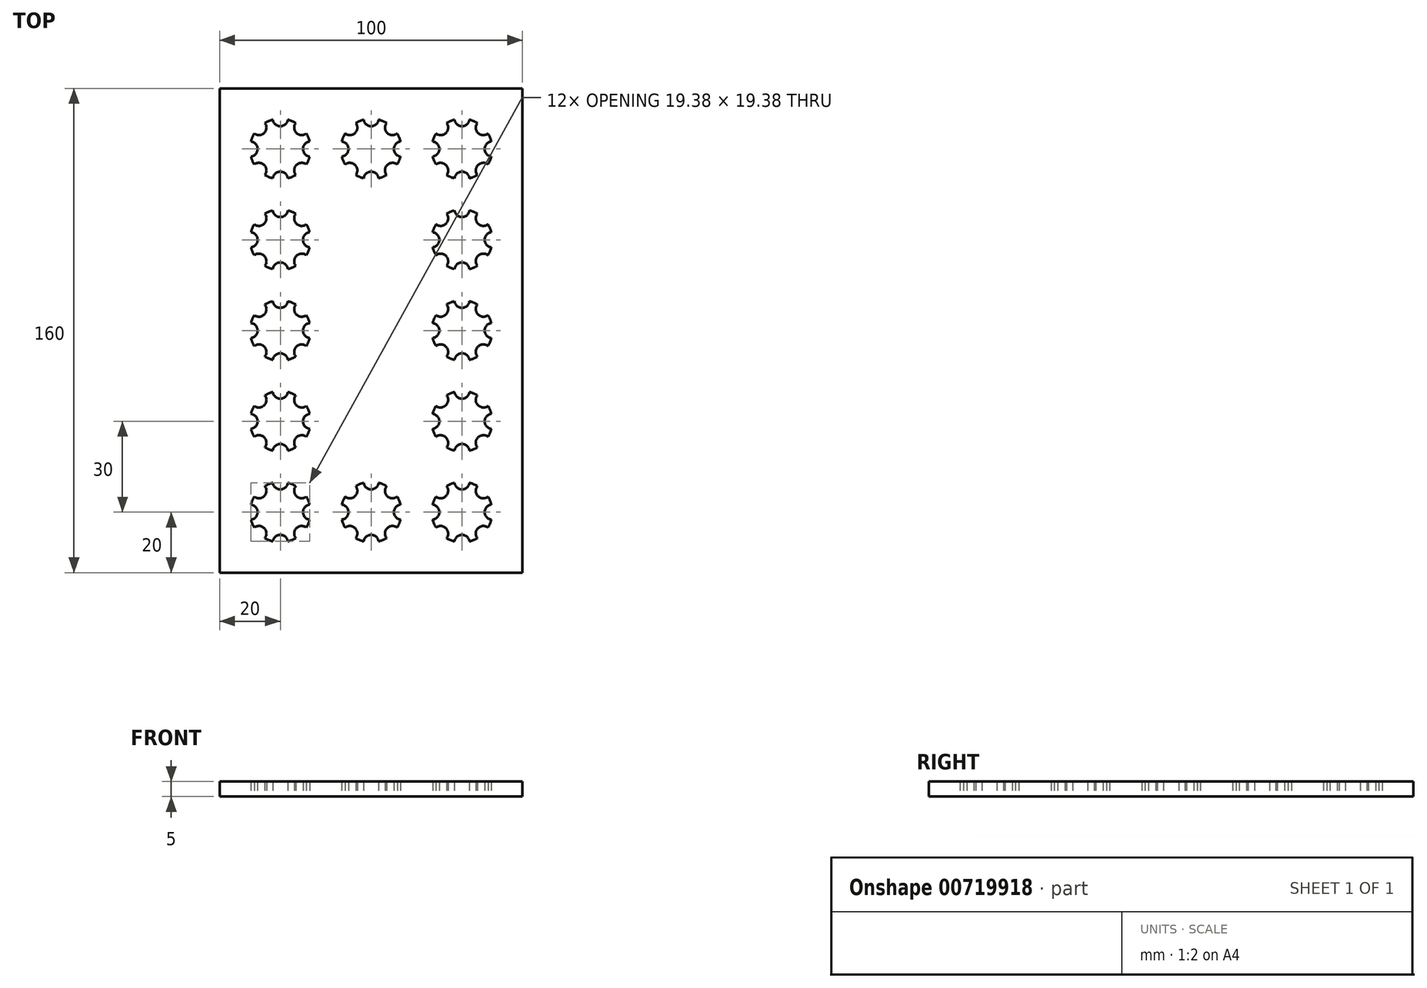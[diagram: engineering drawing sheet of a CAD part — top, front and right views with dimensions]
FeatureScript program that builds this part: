
annotation { "Feature Type Name" : "Feature", "Feature Type Description" : "" }
export const myFeature = defineFeature(function(context is Context, id is Id, definition is map)
    precondition{}
    {
        {
            var Q0;
            Q0=qCreatedBy(makeId("Top.planeOp"),FACE);
            var sketch = newSketch(context, id + "F0", { "sketchPlane" : qUnion([Q0])});
            skLineSegment(sketch, "E0.bottom", {"start": v(0, 0) * mm, "end": v(100, 0) * mm});
            skLineSegment(sketch, "E0.top", {"start": v(0, -160) * mm, "end": v(100, -160) * mm});
            skLineSegment(sketch, "E0.left", {"start": v(0, 0) * mm, "end": v(0, -160) * mm});
            skLineSegment(sketch, "E0.right", {"start": v(100, 0) * mm, "end": v(100, -160) * mm});
            skArc(sketch, "E1", {"start": v(25.1, -11.4) * mm, "mid": v(23.83, -10.76) * mm, "end": v(22.48, -10.31) * mm});
            skArc(sketch, "E2", {"start": v(17.52, -10.31) * mm, "mid": v(20, -12.5) * mm, "end": v(22.48, -10.31) * mm});
            skArc(sketch, "E3.1.0", {"start": v(11.4, -14.9) * mm, "mid": v(14.7, -14.7) * mm, "end": v(14.9, -11.4) * mm});
            skArc(sketch, "E3.2.0", {"start": v(10.31, -22.48) * mm, "mid": v(12.5, -20) * mm, "end": v(10.31, -17.52) * mm});
            skArc(sketch, "E3.3.0", {"start": v(14.9, -28.6) * mm, "mid": v(14.7, -25.3) * mm, "end": v(11.4, -25.1) * mm});
            skArc(sketch, "E3.4.0", {"start": v(22.48, -29.69) * mm, "mid": v(20, -27.5) * mm, "end": v(17.52, -29.69) * mm});
            skArc(sketch, "E3.5.0", {"start": v(28.6, -25.1) * mm, "mid": v(25.3, -25.3) * mm, "end": v(25.1, -28.6) * mm});
            skArc(sketch, "E3.6.0", {"start": v(29.69, -17.52) * mm, "mid": v(27.5, -20) * mm, "end": v(29.69, -22.48) * mm});
            skArc(sketch, "E3.7.0", {"start": v(25.1, -11.4) * mm, "mid": v(25.3, -14.7) * mm, "end": v(28.6, -14.9) * mm});
            skArc(sketch, "E4.trimOffspring", {"start": v(29.69, -17.52) * mm, "mid": v(29.24, -16.17) * mm, "end": v(28.6, -14.9) * mm});
            skArc(sketch, "E5.trimOffspring", {"start": v(28.6, -25.1) * mm, "mid": v(29.24, -23.83) * mm, "end": v(29.69, -22.48) * mm});
            skArc(sketch, "E6.trimOffspring", {"start": v(22.48, -29.69) * mm, "mid": v(23.83, -29.24) * mm, "end": v(25.1, -28.6) * mm});
            skArc(sketch, "E7.trimOffspring", {"start": v(14.9, -28.6) * mm, "mid": v(16.17, -29.24) * mm, "end": v(17.52, -29.69) * mm});
            skArc(sketch, "E8.trimOffspring", {"start": v(10.31, -22.48) * mm, "mid": v(10.76, -23.83) * mm, "end": v(11.4, -25.1) * mm});
            skArc(sketch, "E9.trimOffspring", {"start": v(11.4, -14.9) * mm, "mid": v(10.76, -16.17) * mm, "end": v(10.31, -17.52) * mm});
            skArc(sketch, "E10.trimOffspring", {"start": v(17.52, -10.31) * mm, "mid": v(16.17, -10.76) * mm, "end": v(14.9, -11.4) * mm});
            skArc(sketch, "E11", {"start": v(25.1, -41.4) * mm, "mid": v(23.83, -40.76) * mm, "end": v(22.48, -40.31) * mm});
            skArc(sketch, "E12", {"start": v(17.52, -40.31) * mm, "mid": v(20, -42.5) * mm, "end": v(22.48, -40.31) * mm});
            skArc(sketch, "E13.1.0", {"start": v(11.4, -44.9) * mm, "mid": v(14.7, -44.7) * mm, "end": v(14.9, -41.4) * mm});
            skArc(sketch, "E13.2.0", {"start": v(10.31, -52.48) * mm, "mid": v(12.5, -50) * mm, "end": v(10.31, -47.52) * mm});
            skArc(sketch, "E13.3.0", {"start": v(14.9, -58.6) * mm, "mid": v(14.7, -55.3) * mm, "end": v(11.4, -55.1) * mm});
            skArc(sketch, "E13.4.0", {"start": v(22.48, -59.69) * mm, "mid": v(20, -57.5) * mm, "end": v(17.52, -59.69) * mm});
            skArc(sketch, "E13.5.0", {"start": v(28.6, -55.1) * mm, "mid": v(25.3, -55.3) * mm, "end": v(25.1, -58.6) * mm});
            skArc(sketch, "E13.6.0", {"start": v(29.69, -47.52) * mm, "mid": v(27.5, -50) * mm, "end": v(29.69, -52.48) * mm});
            skArc(sketch, "E13.7.0", {"start": v(25.1, -41.4) * mm, "mid": v(25.3, -44.7) * mm, "end": v(28.6, -44.9) * mm});
            skArc(sketch, "E14.trimOffspring", {"start": v(29.69, -47.52) * mm, "mid": v(29.24, -46.17) * mm, "end": v(28.6, -44.9) * mm});
            skArc(sketch, "E15.trimOffspring", {"start": v(28.6, -55.1) * mm, "mid": v(29.24, -53.83) * mm, "end": v(29.69, -52.48) * mm});
            skArc(sketch, "E16.trimOffspring", {"start": v(22.48, -59.69) * mm, "mid": v(23.83, -59.24) * mm, "end": v(25.1, -58.6) * mm});
            skArc(sketch, "E17.trimOffspring", {"start": v(14.9, -58.6) * mm, "mid": v(16.17, -59.24) * mm, "end": v(17.52, -59.69) * mm});
            skArc(sketch, "E18.trimOffspring", {"start": v(10.31, -52.48) * mm, "mid": v(10.76, -53.83) * mm, "end": v(11.4, -55.1) * mm});
            skArc(sketch, "E19.trimOffspring", {"start": v(11.4, -44.9) * mm, "mid": v(10.76, -46.17) * mm, "end": v(10.31, -47.52) * mm});
            skArc(sketch, "E20.trimOffspring", {"start": v(17.52, -40.31) * mm, "mid": v(16.17, -40.76) * mm, "end": v(14.9, -41.4) * mm});
            skArc(sketch, "E21", {"start": v(25.1, -71.4) * mm, "mid": v(23.83, -70.76) * mm, "end": v(22.48, -70.31) * mm});
            skArc(sketch, "E22", {"start": v(17.52, -70.31) * mm, "mid": v(20, -72.5) * mm, "end": v(22.48, -70.31) * mm});
            skArc(sketch, "E23.1.0", {"start": v(11.4, -74.9) * mm, "mid": v(14.7, -74.7) * mm, "end": v(14.9, -71.4) * mm});
            skArc(sketch, "E23.2.0", {"start": v(10.31, -82.48) * mm, "mid": v(12.5, -80) * mm, "end": v(10.31, -77.52) * mm});
            skArc(sketch, "E23.3.0", {"start": v(14.9, -88.6) * mm, "mid": v(14.7, -85.3) * mm, "end": v(11.4, -85.1) * mm});
            skArc(sketch, "E23.4.0", {"start": v(22.48, -89.69) * mm, "mid": v(20, -87.5) * mm, "end": v(17.52, -89.69) * mm});
            skArc(sketch, "E23.5.0", {"start": v(28.6, -85.1) * mm, "mid": v(25.3, -85.3) * mm, "end": v(25.1, -88.6) * mm});
            skArc(sketch, "E23.6.0", {"start": v(29.69, -77.52) * mm, "mid": v(27.5, -80) * mm, "end": v(29.69, -82.48) * mm});
            skArc(sketch, "E23.7.0", {"start": v(25.1, -71.4) * mm, "mid": v(25.3, -74.7) * mm, "end": v(28.6, -74.9) * mm});
            skArc(sketch, "E24.trimOffspring", {"start": v(29.69, -77.52) * mm, "mid": v(29.24, -76.17) * mm, "end": v(28.6, -74.9) * mm});
            skArc(sketch, "E25.trimOffspring", {"start": v(28.6, -85.1) * mm, "mid": v(29.24, -83.83) * mm, "end": v(29.69, -82.48) * mm});
            skArc(sketch, "E26.trimOffspring", {"start": v(22.48, -89.69) * mm, "mid": v(23.83, -89.24) * mm, "end": v(25.1, -88.6) * mm});
            skArc(sketch, "E27.trimOffspring", {"start": v(14.9, -88.6) * mm, "mid": v(16.17, -89.24) * mm, "end": v(17.52, -89.69) * mm});
            skArc(sketch, "E28.trimOffspring", {"start": v(10.31, -82.48) * mm, "mid": v(10.76, -83.83) * mm, "end": v(11.4, -85.1) * mm});
            skArc(sketch, "E29.trimOffspring", {"start": v(11.4, -74.9) * mm, "mid": v(10.76, -76.17) * mm, "end": v(10.31, -77.52) * mm});
            skArc(sketch, "E30.trimOffspring", {"start": v(17.52, -70.31) * mm, "mid": v(16.17, -70.76) * mm, "end": v(14.9, -71.4) * mm});
            skArc(sketch, "E31", {"start": v(25.1, -101.4) * mm, "mid": v(23.83, -100.76) * mm, "end": v(22.48, -100.31) * mm});
            skArc(sketch, "E32", {"start": v(17.52, -100.31) * mm, "mid": v(20, -102.5) * mm, "end": v(22.48, -100.31) * mm});
            skArc(sketch, "E33.1.0", {"start": v(11.4, -104.9) * mm, "mid": v(14.7, -104.7) * mm, "end": v(14.9, -101.4) * mm});
            skArc(sketch, "E33.2.0", {"start": v(10.31, -112.48) * mm, "mid": v(12.5, -110) * mm, "end": v(10.31, -107.52) * mm});
            skArc(sketch, "E33.3.0", {"start": v(14.9, -118.6) * mm, "mid": v(14.7, -115.3) * mm, "end": v(11.4, -115.1) * mm});
            skArc(sketch, "E33.4.0", {"start": v(22.48, -119.69) * mm, "mid": v(20, -117.5) * mm, "end": v(17.52, -119.69) * mm});
            skArc(sketch, "E33.5.0", {"start": v(28.6, -115.1) * mm, "mid": v(25.3, -115.3) * mm, "end": v(25.1, -118.6) * mm});
            skArc(sketch, "E33.6.0", {"start": v(29.69, -107.52) * mm, "mid": v(27.5, -110) * mm, "end": v(29.69, -112.48) * mm});
            skArc(sketch, "E33.7.0", {"start": v(25.1, -101.4) * mm, "mid": v(25.3, -104.7) * mm, "end": v(28.6, -104.9) * mm});
            skArc(sketch, "E34.trimOffspring", {"start": v(29.69, -107.52) * mm, "mid": v(29.24, -106.17) * mm, "end": v(28.6, -104.9) * mm});
            skArc(sketch, "E35.trimOffspring", {"start": v(28.6, -115.1) * mm, "mid": v(29.24, -113.83) * mm, "end": v(29.69, -112.48) * mm});
            skArc(sketch, "E36.trimOffspring", {"start": v(22.48, -119.69) * mm, "mid": v(23.83, -119.24) * mm, "end": v(25.1, -118.6) * mm});
            skArc(sketch, "E37.trimOffspring", {"start": v(14.9, -118.6) * mm, "mid": v(16.17, -119.24) * mm, "end": v(17.52, -119.69) * mm});
            skArc(sketch, "E38.trimOffspring", {"start": v(10.31, -112.48) * mm, "mid": v(10.76, -113.83) * mm, "end": v(11.4, -115.1) * mm});
            skArc(sketch, "E39.trimOffspring", {"start": v(11.4, -104.9) * mm, "mid": v(10.76, -106.17) * mm, "end": v(10.31, -107.52) * mm});
            skArc(sketch, "E40.trimOffspring", {"start": v(17.52, -100.31) * mm, "mid": v(16.17, -100.76) * mm, "end": v(14.9, -101.4) * mm});
            skArc(sketch, "E41", {"start": v(25.1, -131.4) * mm, "mid": v(23.83, -130.76) * mm, "end": v(22.48, -130.31) * mm});
            skArc(sketch, "E42", {"start": v(17.52, -130.31) * mm, "mid": v(20, -132.5) * mm, "end": v(22.48, -130.31) * mm});
            skArc(sketch, "E43.1.0", {"start": v(11.4, -134.9) * mm, "mid": v(14.7, -134.7) * mm, "end": v(14.9, -131.4) * mm});
            skArc(sketch, "E43.2.0", {"start": v(10.31, -142.48) * mm, "mid": v(12.5, -140) * mm, "end": v(10.31, -137.52) * mm});
            skArc(sketch, "E43.3.0", {"start": v(14.9, -148.6) * mm, "mid": v(14.7, -145.3) * mm, "end": v(11.4, -145.1) * mm});
            skArc(sketch, "E43.4.0", {"start": v(22.48, -149.69) * mm, "mid": v(20, -147.5) * mm, "end": v(17.52, -149.69) * mm});
            skArc(sketch, "E43.5.0", {"start": v(28.6, -145.1) * mm, "mid": v(25.3, -145.3) * mm, "end": v(25.1, -148.6) * mm});
            skArc(sketch, "E43.6.0", {"start": v(29.69, -137.52) * mm, "mid": v(27.5, -140) * mm, "end": v(29.69, -142.48) * mm});
            skArc(sketch, "E43.7.0", {"start": v(25.1, -131.4) * mm, "mid": v(25.3, -134.7) * mm, "end": v(28.6, -134.9) * mm});
            skArc(sketch, "E44.trimOffspring", {"start": v(29.69, -137.52) * mm, "mid": v(29.24, -136.17) * mm, "end": v(28.6, -134.9) * mm});
            skArc(sketch, "E45.trimOffspring", {"start": v(28.6, -145.1) * mm, "mid": v(29.24, -143.83) * mm, "end": v(29.69, -142.48) * mm});
            skArc(sketch, "E46.trimOffspring", {"start": v(22.48, -149.69) * mm, "mid": v(23.83, -149.24) * mm, "end": v(25.1, -148.6) * mm});
            skArc(sketch, "E47.trimOffspring", {"start": v(14.9, -148.6) * mm, "mid": v(16.17, -149.24) * mm, "end": v(17.52, -149.69) * mm});
            skArc(sketch, "E48.trimOffspring", {"start": v(10.31, -142.48) * mm, "mid": v(10.76, -143.83) * mm, "end": v(11.4, -145.1) * mm});
            skArc(sketch, "E49.trimOffspring", {"start": v(11.4, -134.9) * mm, "mid": v(10.76, -136.17) * mm, "end": v(10.31, -137.52) * mm});
            skArc(sketch, "E50.trimOffspring", {"start": v(17.52, -130.31) * mm, "mid": v(16.17, -130.76) * mm, "end": v(14.9, -131.4) * mm});
            skArc(sketch, "E51", {"start": v(55.1, -131.4) * mm, "mid": v(53.83, -130.76) * mm, "end": v(52.48, -130.31) * mm});
            skArc(sketch, "E52", {"start": v(47.52, -130.31) * mm, "mid": v(50, -132.5) * mm, "end": v(52.48, -130.31) * mm});
            skArc(sketch, "E53.1.0", {"start": v(41.4, -134.9) * mm, "mid": v(44.7, -134.7) * mm, "end": v(44.9, -131.4) * mm});
            skArc(sketch, "E53.2.0", {"start": v(40.31, -142.48) * mm, "mid": v(42.5, -140) * mm, "end": v(40.31, -137.52) * mm});
            skArc(sketch, "E53.3.0", {"start": v(44.9, -148.6) * mm, "mid": v(44.7, -145.3) * mm, "end": v(41.4, -145.1) * mm});
            skArc(sketch, "E53.4.0", {"start": v(52.48, -149.69) * mm, "mid": v(50, -147.5) * mm, "end": v(47.52, -149.69) * mm});
            skArc(sketch, "E53.5.0", {"start": v(58.6, -145.1) * mm, "mid": v(55.3, -145.3) * mm, "end": v(55.1, -148.6) * mm});
            skArc(sketch, "E53.6.0", {"start": v(59.69, -137.52) * mm, "mid": v(57.5, -140) * mm, "end": v(59.69, -142.48) * mm});
            skArc(sketch, "E53.7.0", {"start": v(55.1, -131.4) * mm, "mid": v(55.3, -134.7) * mm, "end": v(58.6, -134.9) * mm});
            skArc(sketch, "E54.trimOffspring", {"start": v(59.69, -137.52) * mm, "mid": v(59.24, -136.17) * mm, "end": v(58.6, -134.9) * mm});
            skArc(sketch, "E55.trimOffspring", {"start": v(58.6, -145.1) * mm, "mid": v(59.24, -143.83) * mm, "end": v(59.69, -142.48) * mm});
            skArc(sketch, "E56.trimOffspring", {"start": v(52.48, -149.69) * mm, "mid": v(53.83, -149.24) * mm, "end": v(55.1, -148.6) * mm});
            skArc(sketch, "E57.trimOffspring", {"start": v(44.9, -148.6) * mm, "mid": v(46.17, -149.24) * mm, "end": v(47.52, -149.69) * mm});
            skArc(sketch, "E58.trimOffspring", {"start": v(40.31, -142.48) * mm, "mid": v(40.76, -143.83) * mm, "end": v(41.4, -145.1) * mm});
            skArc(sketch, "E59.trimOffspring", {"start": v(41.4, -134.9) * mm, "mid": v(40.76, -136.17) * mm, "end": v(40.31, -137.52) * mm});
            skArc(sketch, "E60.trimOffspring", {"start": v(47.52, -130.31) * mm, "mid": v(46.17, -130.76) * mm, "end": v(44.9, -131.4) * mm});
            skArc(sketch, "E61", {"start": v(85.1, -131.4) * mm, "mid": v(83.83, -130.76) * mm, "end": v(82.48, -130.31) * mm});
            skArc(sketch, "E62", {"start": v(77.52, -130.31) * mm, "mid": v(80, -132.5) * mm, "end": v(82.48, -130.31) * mm});
            skArc(sketch, "E63.1.0", {"start": v(71.4, -134.9) * mm, "mid": v(74.7, -134.7) * mm, "end": v(74.9, -131.4) * mm});
            skArc(sketch, "E63.2.0", {"start": v(70.31, -142.48) * mm, "mid": v(72.5, -140) * mm, "end": v(70.31, -137.52) * mm});
            skArc(sketch, "E63.3.0", {"start": v(74.9, -148.6) * mm, "mid": v(74.7, -145.3) * mm, "end": v(71.4, -145.1) * mm});
            skArc(sketch, "E63.4.0", {"start": v(82.48, -149.69) * mm, "mid": v(80, -147.5) * mm, "end": v(77.52, -149.69) * mm});
            skArc(sketch, "E63.5.0", {"start": v(88.6, -145.1) * mm, "mid": v(85.3, -145.3) * mm, "end": v(85.1, -148.6) * mm});
            skArc(sketch, "E63.6.0", {"start": v(89.69, -137.52) * mm, "mid": v(87.5, -140) * mm, "end": v(89.69, -142.48) * mm});
            skArc(sketch, "E63.7.0", {"start": v(85.1, -131.4) * mm, "mid": v(85.3, -134.7) * mm, "end": v(88.6, -134.9) * mm});
            skArc(sketch, "E64.trimOffspring", {"start": v(89.69, -137.52) * mm, "mid": v(89.24, -136.17) * mm, "end": v(88.6, -134.9) * mm});
            skArc(sketch, "E65.trimOffspring", {"start": v(88.6, -145.1) * mm, "mid": v(89.24, -143.83) * mm, "end": v(89.69, -142.48) * mm});
            skArc(sketch, "E66.trimOffspring", {"start": v(82.48, -149.69) * mm, "mid": v(83.83, -149.24) * mm, "end": v(85.1, -148.6) * mm});
            skArc(sketch, "E67.trimOffspring", {"start": v(74.9, -148.6) * mm, "mid": v(76.17, -149.24) * mm, "end": v(77.52, -149.69) * mm});
            skArc(sketch, "E68.trimOffspring", {"start": v(70.31, -142.48) * mm, "mid": v(70.76, -143.83) * mm, "end": v(71.4, -145.1) * mm});
            skArc(sketch, "E69.trimOffspring", {"start": v(71.4, -134.9) * mm, "mid": v(70.76, -136.17) * mm, "end": v(70.31, -137.52) * mm});
            skArc(sketch, "E70.trimOffspring", {"start": v(77.52, -130.31) * mm, "mid": v(76.17, -130.76) * mm, "end": v(74.9, -131.4) * mm});
            skArc(sketch, "E71", {"start": v(85.1, -101.4) * mm, "mid": v(83.83, -100.76) * mm, "end": v(82.48, -100.31) * mm});
            skArc(sketch, "E72", {"start": v(77.52, -100.31) * mm, "mid": v(80, -102.5) * mm, "end": v(82.48, -100.31) * mm});
            skArc(sketch, "E73.1.0", {"start": v(71.4, -104.9) * mm, "mid": v(74.7, -104.7) * mm, "end": v(74.9, -101.4) * mm});
            skArc(sketch, "E73.2.0", {"start": v(70.31, -112.48) * mm, "mid": v(72.5, -110) * mm, "end": v(70.31, -107.52) * mm});
            skArc(sketch, "E73.3.0", {"start": v(74.9, -118.6) * mm, "mid": v(74.7, -115.3) * mm, "end": v(71.4, -115.1) * mm});
            skArc(sketch, "E73.4.0", {"start": v(82.48, -119.69) * mm, "mid": v(80, -117.5) * mm, "end": v(77.52, -119.69) * mm});
            skArc(sketch, "E73.5.0", {"start": v(88.6, -115.1) * mm, "mid": v(85.3, -115.3) * mm, "end": v(85.1, -118.6) * mm});
            skArc(sketch, "E73.6.0", {"start": v(89.69, -107.52) * mm, "mid": v(87.5, -110) * mm, "end": v(89.69, -112.48) * mm});
            skArc(sketch, "E73.7.0", {"start": v(85.1, -101.4) * mm, "mid": v(85.3, -104.7) * mm, "end": v(88.6, -104.9) * mm});
            skArc(sketch, "E74.trimOffspring", {"start": v(89.69, -107.52) * mm, "mid": v(89.24, -106.17) * mm, "end": v(88.6, -104.9) * mm});
            skArc(sketch, "E75.trimOffspring", {"start": v(88.6, -115.1) * mm, "mid": v(89.24, -113.83) * mm, "end": v(89.69, -112.48) * mm});
            skArc(sketch, "E76.trimOffspring", {"start": v(82.48, -119.69) * mm, "mid": v(83.83, -119.24) * mm, "end": v(85.1, -118.6) * mm});
            skArc(sketch, "E77.trimOffspring", {"start": v(74.9, -118.6) * mm, "mid": v(76.17, -119.24) * mm, "end": v(77.52, -119.69) * mm});
            skArc(sketch, "E78.trimOffspring", {"start": v(70.31, -112.48) * mm, "mid": v(70.76, -113.83) * mm, "end": v(71.4, -115.1) * mm});
            skArc(sketch, "E79.trimOffspring", {"start": v(71.4, -104.9) * mm, "mid": v(70.76, -106.17) * mm, "end": v(70.31, -107.52) * mm});
            skArc(sketch, "E80.trimOffspring", {"start": v(77.52, -100.31) * mm, "mid": v(76.17, -100.76) * mm, "end": v(74.9, -101.4) * mm});
            skArc(sketch, "E81", {"start": v(85.1, -71.4) * mm, "mid": v(83.83, -70.76) * mm, "end": v(82.48, -70.31) * mm});
            skArc(sketch, "E82", {"start": v(77.52, -70.31) * mm, "mid": v(80, -72.5) * mm, "end": v(82.48, -70.31) * mm});
            skArc(sketch, "E83.1.0", {"start": v(71.4, -74.9) * mm, "mid": v(74.7, -74.7) * mm, "end": v(74.9, -71.4) * mm});
            skArc(sketch, "E83.2.0", {"start": v(70.31, -82.48) * mm, "mid": v(72.5, -80) * mm, "end": v(70.31, -77.52) * mm});
            skArc(sketch, "E83.3.0", {"start": v(74.9, -88.6) * mm, "mid": v(74.7, -85.3) * mm, "end": v(71.4, -85.1) * mm});
            skArc(sketch, "E83.4.0", {"start": v(82.48, -89.69) * mm, "mid": v(80, -87.5) * mm, "end": v(77.52, -89.69) * mm});
            skArc(sketch, "E83.5.0", {"start": v(88.6, -85.1) * mm, "mid": v(85.3, -85.3) * mm, "end": v(85.1, -88.6) * mm});
            skArc(sketch, "E83.6.0", {"start": v(89.69, -77.52) * mm, "mid": v(87.5, -80) * mm, "end": v(89.69, -82.48) * mm});
            skArc(sketch, "E83.7.0", {"start": v(85.1, -71.4) * mm, "mid": v(85.3, -74.7) * mm, "end": v(88.6, -74.9) * mm});
            skArc(sketch, "E84.trimOffspring", {"start": v(89.69, -77.52) * mm, "mid": v(89.24, -76.17) * mm, "end": v(88.6, -74.9) * mm});
            skArc(sketch, "E85.trimOffspring", {"start": v(88.6, -85.1) * mm, "mid": v(89.24, -83.83) * mm, "end": v(89.69, -82.48) * mm});
            skArc(sketch, "E86.trimOffspring", {"start": v(82.48, -89.69) * mm, "mid": v(83.83, -89.24) * mm, "end": v(85.1, -88.6) * mm});
            skArc(sketch, "E87.trimOffspring", {"start": v(74.9, -88.6) * mm, "mid": v(76.17, -89.24) * mm, "end": v(77.52, -89.69) * mm});
            skArc(sketch, "E88.trimOffspring", {"start": v(70.31, -82.48) * mm, "mid": v(70.76, -83.83) * mm, "end": v(71.4, -85.1) * mm});
            skArc(sketch, "E89.trimOffspring", {"start": v(71.4, -74.9) * mm, "mid": v(70.76, -76.17) * mm, "end": v(70.31, -77.52) * mm});
            skArc(sketch, "E90.trimOffspring", {"start": v(77.52, -70.31) * mm, "mid": v(76.17, -70.76) * mm, "end": v(74.9, -71.4) * mm});
            skArc(sketch, "E91", {"start": v(85.1, -41.4) * mm, "mid": v(83.83, -40.76) * mm, "end": v(82.48, -40.31) * mm});
            skArc(sketch, "E92", {"start": v(77.52, -40.31) * mm, "mid": v(80, -42.5) * mm, "end": v(82.48, -40.31) * mm});
            skArc(sketch, "E93.1.0", {"start": v(71.4, -44.9) * mm, "mid": v(74.7, -44.7) * mm, "end": v(74.9, -41.4) * mm});
            skArc(sketch, "E93.2.0", {"start": v(70.31, -52.48) * mm, "mid": v(72.5, -50) * mm, "end": v(70.31, -47.52) * mm});
            skArc(sketch, "E93.3.0", {"start": v(74.9, -58.6) * mm, "mid": v(74.7, -55.3) * mm, "end": v(71.4, -55.1) * mm});
            skArc(sketch, "E93.4.0", {"start": v(82.48, -59.69) * mm, "mid": v(80, -57.5) * mm, "end": v(77.52, -59.69) * mm});
            skArc(sketch, "E93.5.0", {"start": v(88.6, -55.1) * mm, "mid": v(85.3, -55.3) * mm, "end": v(85.1, -58.6) * mm});
            skArc(sketch, "E93.6.0", {"start": v(89.69, -47.52) * mm, "mid": v(87.5, -50) * mm, "end": v(89.69, -52.48) * mm});
            skArc(sketch, "E93.7.0", {"start": v(85.1, -41.4) * mm, "mid": v(85.3, -44.7) * mm, "end": v(88.6, -44.9) * mm});
            skArc(sketch, "E94.trimOffspring", {"start": v(89.69, -47.52) * mm, "mid": v(89.24, -46.17) * mm, "end": v(88.6, -44.9) * mm});
            skArc(sketch, "E95.trimOffspring", {"start": v(88.6, -55.1) * mm, "mid": v(89.24, -53.83) * mm, "end": v(89.69, -52.48) * mm});
            skArc(sketch, "E96.trimOffspring", {"start": v(82.48, -59.69) * mm, "mid": v(83.83, -59.24) * mm, "end": v(85.1, -58.6) * mm});
            skArc(sketch, "E97.trimOffspring", {"start": v(74.9, -58.6) * mm, "mid": v(76.17, -59.24) * mm, "end": v(77.52, -59.69) * mm});
            skArc(sketch, "E98.trimOffspring", {"start": v(70.31, -52.48) * mm, "mid": v(70.76, -53.83) * mm, "end": v(71.4, -55.1) * mm});
            skArc(sketch, "E99.trimOffspring", {"start": v(71.4, -44.9) * mm, "mid": v(70.76, -46.17) * mm, "end": v(70.31, -47.52) * mm});
            skArc(sketch, "E100.trimOffspring", {"start": v(77.52, -40.31) * mm, "mid": v(76.17, -40.76) * mm, "end": v(74.9, -41.4) * mm});
            skArc(sketch, "E101", {"start": v(55.1, -11.4) * mm, "mid": v(53.83, -10.76) * mm, "end": v(52.48, -10.31) * mm});
            skArc(sketch, "E102", {"start": v(47.52, -10.31) * mm, "mid": v(50, -12.5) * mm, "end": v(52.48, -10.31) * mm});
            skArc(sketch, "E103.1.0", {"start": v(41.4, -14.9) * mm, "mid": v(44.7, -14.7) * mm, "end": v(44.9, -11.4) * mm});
            skArc(sketch, "E103.2.0", {"start": v(40.31, -22.48) * mm, "mid": v(42.5, -20) * mm, "end": v(40.31, -17.52) * mm});
            skArc(sketch, "E103.3.0", {"start": v(44.9, -28.6) * mm, "mid": v(44.7, -25.3) * mm, "end": v(41.4, -25.1) * mm});
            skArc(sketch, "E103.4.0", {"start": v(52.48, -29.69) * mm, "mid": v(50, -27.5) * mm, "end": v(47.52, -29.69) * mm});
            skArc(sketch, "E103.5.0", {"start": v(58.6, -25.1) * mm, "mid": v(55.3, -25.3) * mm, "end": v(55.1, -28.6) * mm});
            skArc(sketch, "E103.6.0", {"start": v(59.69, -17.52) * mm, "mid": v(57.5, -20) * mm, "end": v(59.69, -22.48) * mm});
            skArc(sketch, "E103.7.0", {"start": v(55.1, -11.4) * mm, "mid": v(55.3, -14.7) * mm, "end": v(58.6, -14.9) * mm});
            skArc(sketch, "E104.trimOffspring", {"start": v(59.69, -17.52) * mm, "mid": v(59.24, -16.17) * mm, "end": v(58.6, -14.9) * mm});
            skArc(sketch, "E105.trimOffspring", {"start": v(58.6, -25.1) * mm, "mid": v(59.24, -23.83) * mm, "end": v(59.69, -22.48) * mm});
            skArc(sketch, "E106.trimOffspring", {"start": v(52.48, -29.69) * mm, "mid": v(53.83, -29.24) * mm, "end": v(55.1, -28.6) * mm});
            skArc(sketch, "E107.trimOffspring", {"start": v(44.9, -28.6) * mm, "mid": v(46.17, -29.24) * mm, "end": v(47.52, -29.69) * mm});
            skArc(sketch, "E108.trimOffspring", {"start": v(40.31, -22.48) * mm, "mid": v(40.76, -23.83) * mm, "end": v(41.4, -25.1) * mm});
            skArc(sketch, "E109.trimOffspring", {"start": v(41.4, -14.9) * mm, "mid": v(40.76, -16.17) * mm, "end": v(40.31, -17.52) * mm});
            skArc(sketch, "E110.trimOffspring", {"start": v(47.52, -10.31) * mm, "mid": v(46.17, -10.76) * mm, "end": v(44.9, -11.4) * mm});
            skArc(sketch, "E111", {"start": v(85.1, -11.4) * mm, "mid": v(83.83, -10.76) * mm, "end": v(82.48, -10.31) * mm});
            skArc(sketch, "E112", {"start": v(77.52, -10.31) * mm, "mid": v(80, -12.5) * mm, "end": v(82.48, -10.31) * mm});
            skArc(sketch, "E113.1.0", {"start": v(71.4, -14.9) * mm, "mid": v(74.7, -14.7) * mm, "end": v(74.9, -11.4) * mm});
            skArc(sketch, "E113.2.0", {"start": v(70.31, -22.48) * mm, "mid": v(72.5, -20) * mm, "end": v(70.31, -17.52) * mm});
            skArc(sketch, "E113.3.0", {"start": v(74.9, -28.6) * mm, "mid": v(74.7, -25.3) * mm, "end": v(71.4, -25.1) * mm});
            skArc(sketch, "E113.4.0", {"start": v(82.48, -29.69) * mm, "mid": v(80, -27.5) * mm, "end": v(77.52, -29.69) * mm});
            skArc(sketch, "E113.5.0", {"start": v(88.6, -25.1) * mm, "mid": v(85.3, -25.3) * mm, "end": v(85.1, -28.6) * mm});
            skArc(sketch, "E113.6.0", {"start": v(89.69, -17.52) * mm, "mid": v(87.5, -20) * mm, "end": v(89.69, -22.48) * mm});
            skArc(sketch, "E113.7.0", {"start": v(85.1, -11.4) * mm, "mid": v(85.3, -14.7) * mm, "end": v(88.6, -14.9) * mm});
            skArc(sketch, "E114.trimOffspring", {"start": v(89.69, -17.52) * mm, "mid": v(89.24, -16.17) * mm, "end": v(88.6, -14.9) * mm});
            skArc(sketch, "E115.trimOffspring", {"start": v(88.6, -25.1) * mm, "mid": v(89.24, -23.83) * mm, "end": v(89.69, -22.48) * mm});
            skArc(sketch, "E116.trimOffspring", {"start": v(82.48, -29.69) * mm, "mid": v(83.83, -29.24) * mm, "end": v(85.1, -28.6) * mm});
            skArc(sketch, "E117.trimOffspring", {"start": v(74.9, -28.6) * mm, "mid": v(76.17, -29.24) * mm, "end": v(77.52, -29.69) * mm});
            skArc(sketch, "E118.trimOffspring", {"start": v(70.31, -22.48) * mm, "mid": v(70.76, -23.83) * mm, "end": v(71.4, -25.1) * mm});
            skArc(sketch, "E119.trimOffspring", {"start": v(71.4, -14.9) * mm, "mid": v(70.76, -16.17) * mm, "end": v(70.31, -17.52) * mm});
            skArc(sketch, "E120.trimOffspring", {"start": v(77.52, -10.31) * mm, "mid": v(76.17, -10.76) * mm, "end": v(74.9, -11.4) * mm});
            skSolve(sketch);
        }
        {
            var Q0;
            Q0 = qSketchRegion(id + "F0", true);
            extrude(context, id + "F1", {"entities" : qUnion([Q0]), "depth" : 5 * mm, "offsetDistance" : 25 * mm});
        }
    });
